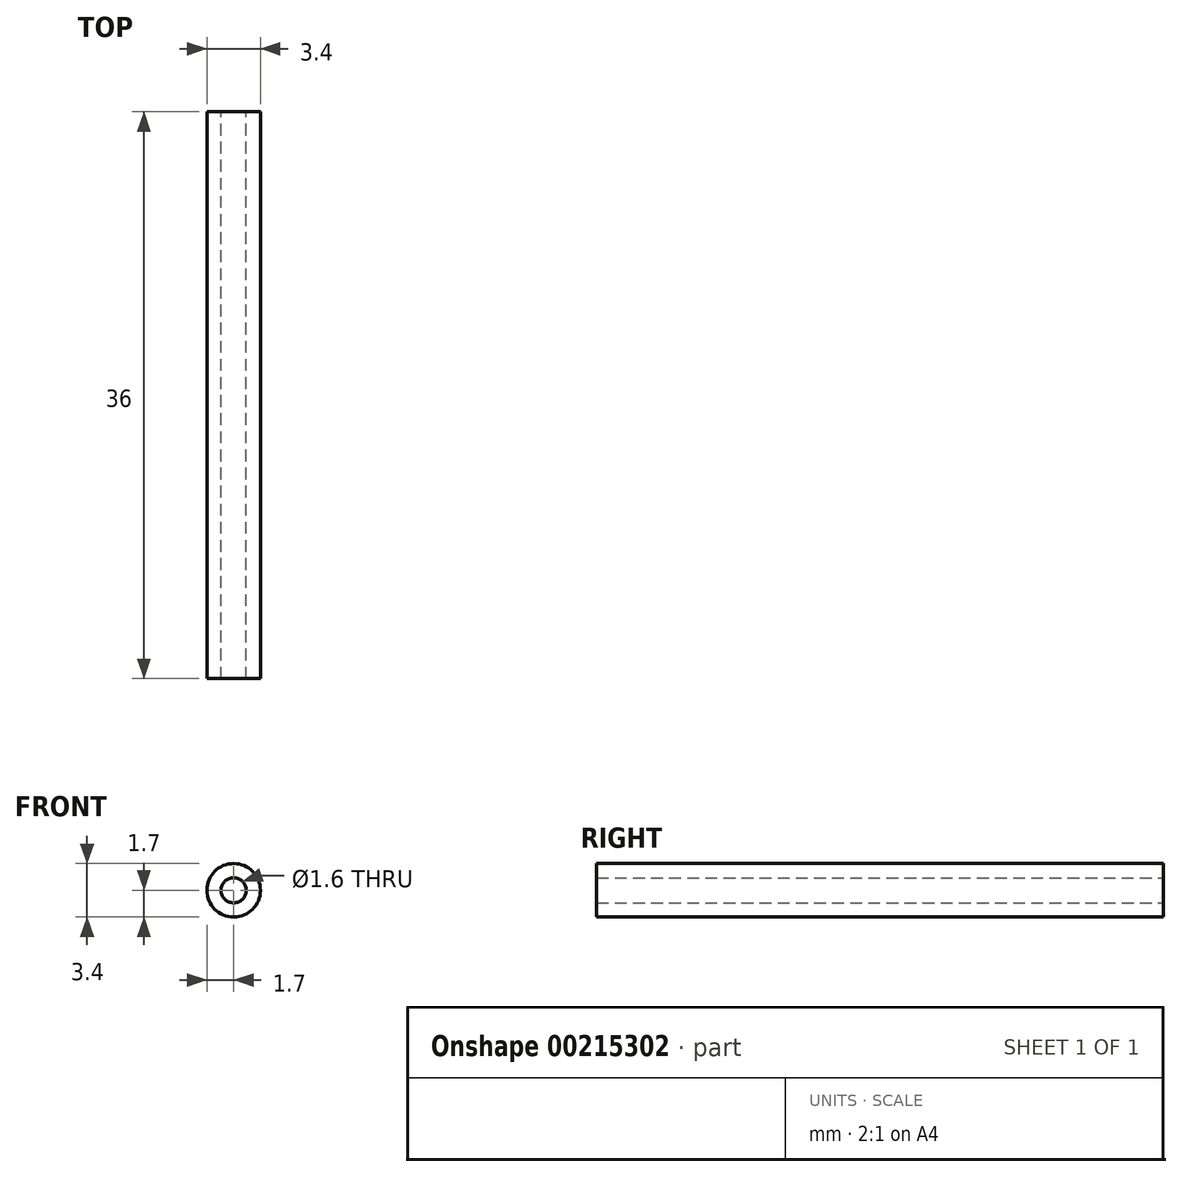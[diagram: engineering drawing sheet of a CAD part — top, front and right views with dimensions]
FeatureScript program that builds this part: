
annotation { "Feature Type Name" : "Feature", "Feature Type Description" : "" }
export const myFeature = defineFeature(function(context is Context, id is Id, definition is map)
    precondition{}
    {
        {
            var Q0;
            Q0=qCreatedBy(makeId("Front.planeOp"),FACE);
            var sketch = newSketch(context, id + "F0", { "sketchPlane" : qUnion([Q0])});
            skCircle(sketch, "E0", {"center": v(0, 0) * mm, "radius": 1.7 * mm});
            skCircle(sketch, "E1", {"center": v(0, 0) * mm, "radius": 0.8 * mm});
            skSolve(sketch);
        }
        {
            var Q0;
            Q0=makeQuery(id+"F0.imprint","IMPRINT",FACE,{"disambiguationData":[TD([[makeQuery(id+"F0.imprint","IMPRINT",EDGE,{"derivedFrom":sQuery(id+"F0.wireOp",EDGE,"E0")}),1.0]])]});
            extrude(context, id + "F1", {"entities" : qUnion([Q0]), "depth" : 36 * mm});
        }
    });
